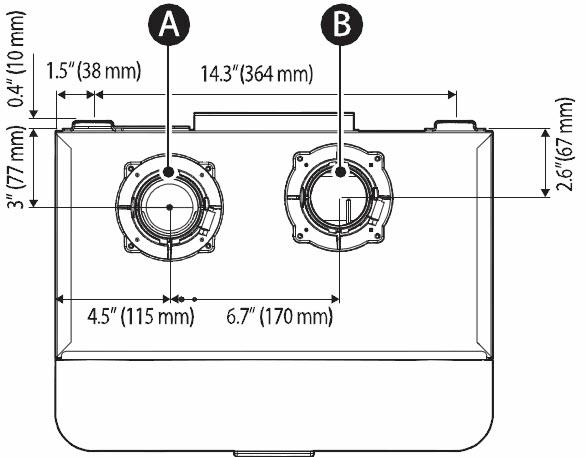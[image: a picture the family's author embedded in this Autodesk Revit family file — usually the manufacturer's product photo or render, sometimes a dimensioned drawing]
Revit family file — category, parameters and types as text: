
# Revit family: Water_Heater-Racks-Navien-NPE-10_Unit_Front---
name_source: partatom
category: Mechanical Equipment
revit_build: Autodesk Revit 2016 (Build: 20150220_1215(x64)
units: mm (PartAtom-declared; Revit-internal decimal feet)

## family parameters
Cut with Voids When Loaded = No
Host = Face
OmniClass Number = 23.65.35.11
OmniClass Title = Supply Water Heaters
Part Type = Normal
Room Calculation Point = No
Round Connector Dimension = Use Diameter
Shared = No

## types (4) — shared parameters
2" Exhaust/Intake = Yes
3" Exhaust/Intake = No
Apparent Load = 0 VA
Assembly Code = D3010500
Certifications = Energy Star | AHRI | CSA | CSA | NFS
Cold Water Inlet = 1"
Configuration = NPE_F10_3F2F_3F2F
Default Elevation = 48 "
Depth = 23.8 "
Description = 10 Unit Front
Exhaust = 2"
Finish = Metal - Navien - White
Flow Rate = 1 GPM
Flow Rate Note = 35°F (19°C) temp rise: 11.2 GPM (42 L/m) | 45°F (25°C) temp rise: 8.7 GPM (33 L/m) | 67°F (36°C) temp rise: NPE-240A: 5.6 GPM(21 L/m), NPE-240S: 5.7 GPM(22 L/m)
Frequency = 60 Hz
Gas Inlet = 1"
Heating Capacity = 120000.0 Btu/h
Heating Capacity Note = 19,900–199,900 (BTU/H)
Height = 65.5 "
Hot Water Outlet = 1"
Ignition = Electronic ignition
Installation Type = Indoor
Intake = 2"
Keynote = 22 33 00.A1
Manifold(s) = (2) 30019040A + (2) 30019041A
Manufacturer = Navien, Inc.
Manufacturer Fax Number = (949) 420-0430
Natural Gas Manifold Pressure = -0.05" WC to -0.58" WC
Natural Gas Supply Pressure = 3.5"–10.5" WC
Number of Poles = 1
Phase = 1
Power Factor = 1
Product Documentation Link = https://www.navieninc.com
Product Name = NPE Series Tankless Water Heaters w/ Racks
Product Page URL = https://www.navieninc.com
Propane Gas Manifold Pressure = -0.10" WC to -0.78" WC
Propane Gas Supply Pressure = 8"–13" WC
Rack(s) = (2) GFFM-KDIZUS-003 + (8) GFFM-KDIZUS-004
Required Cascade Operation Accessory = (10) 30014367A (Common Vent Damper & Cascade Communication Cable) or (9) GXXX000546 (Individual Vent Cascade Communication Cable)
URL = https://www.navieninc.com
Venting = Exhaust: 2" PVC, CPVC, PP, SS / 2" special gas vent type BH (Class II, A/B/C) | Intake: 2" PVC, CPVC, PP, SS / 2" special gas vent type BH (Class II, A/B/C) | Vent clearances: 0" to combustibles
Venting Type = Forced draft direct vent
Version = 2016 - v1.0.a
Voltage = 120 V
Water Pressure = 15–150 PSI
Wi-Fi Ready = NaviLink Wi-Fi Control: PBCM-AS-001
Width = 23.3 "

## per-type parameters (varying)
| type | Constraints | Model | Natural Gas | Propane Gas | Recirculation Inlet | Recirculation Inlet Visibility | Tankless Water Heaters | Weight |
| Natural Gas - Recirculating System - NPE-240A(Advanced)-NG | 6 | (10) NPE-240A-NG | Yes | No | 0" | Yes | (10) NPE-240A-NG | 82.00 lbf |
| Natural Gas - NPE-240S(Standard)-NG | 7 | (10) NPE-240S-NG | Yes | No | 1" | No | (10) NPE-240S-NG | 75.00 lbf |
| Propane Gas - Recirculating System - NPE-240A(Advanced)-LPG | 6 | (10) NPE-240A-LPG | No | Yes | 0" | Yes | (10) NPE-240A-LPG | 82.00 lbf |
| Propane Gas - NPE-240S(Standard)-LPG | 7 | (10) NPE-240S-LPG | No | Yes | 1" | No | (10) NPE-240S-LPG | 75.00 lbf |

## geometry (parser evidence)
native form markers: Sweep x23
no freeform markers — native parametric forms only
